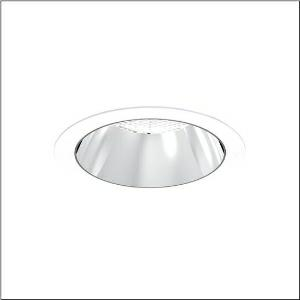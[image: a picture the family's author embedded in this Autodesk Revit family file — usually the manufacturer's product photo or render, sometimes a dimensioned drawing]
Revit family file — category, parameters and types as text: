
# Revit family: lunis_21_xl_51db15mf91c
name_source: partatom
category: Lighting Fixtures
units: mm (PartAtom-declared; Revit-internal decimal feet)

## family parameters
Cut with Voids When Loaded = No
Host = Face
Light Source = No
Part Type = Normal
Room Calculation Point = No
Round Connector Dimension = Use Diameter
Shared = No

## types (1)
- --- (1 x LED, 3740 lm, 21.7 W, 6500K)
    Apparent Load = 22 VA
    CIE Flux Codes = 92 100 100 100 100
    Color Rendering = 80
    Color Temperature = 6500K
    Default Elevation = 1800 mm
    Description = Lunis 21 XL, downlight, light control with lens, of PMMA, anti glare with reflector, of PC, highly specular, light emission: direct distribution, LED rated luminous flux: 2.510lm, light colour: 830/840/865, with terminal, 3-pole, mains connection: 220..240V, AC/DC, 0/50..60Hz, housing, round, of diecast aluminium, traffic white (RAL 9016), diameter: 230mm, clamping range: 1..40mm, protection rating (complete): IP20, protection rating (on room side): IP54, insulation class (complete): insulation class II (safety insulation), certification: CE, impact resistance: IK03, packaging unit: 1 piece
    Height = 0 mm  [stored 0 ft]
    Lamp = 1 x LED
    Lamp Light Flux = 3740 lm
    Lamp Power = 21.7 W
    Lamp count = 1
    Length = 230 mm
    Luminous efficacy = 172 lm/W
    Manufacturer = Siteco
    ModVariant = No
    Model = 51DB15MF91C
    Mounting Place = Ceiling
    Mounting Type = Recessed
    Number of Poles = 1
    OnlyDefault = Yes
    Power Factor = 1
    Product Name = Lunis 21 XL
    Product group = downlight
    ProductGroupID = 401
    Protection Class = Protection class II
    Protection Degree = IP 20
    RLX_Detail_Level = 1
    RLX_Emergency_Light_Flux = 0 lm
    RLX_Emergency_Type = 0
    RLX_Emergency_Type_DB = No
    RlxData = <blob elided: 20061 chars, md5=cb79e4f4>
    Socket = socket
    Standby Power = 0 W
    System Light Flux = 3740 lm
    System Power = 22 W
    Type Comments = individual setting: colour temperature 6500K, luminous flux: 100 % | (OFF | ON | ON | ON) | 650 mA
    Type Image = l_1291156.jpg
    URL = http://relux.com
    VarID = @adj_036199
    Voltage = 0 V
    Weight = 0.00 kg
    Width = 0 mm  [stored 0 ft]

note: [stored X ft] marks values corroborated as IEEE doubles in the binary element streams (Revit-internal decimal feet)

## geometry (parser evidence)
native form markers: Blend x4, Sweep x8
no freeform markers — native parametric forms only
